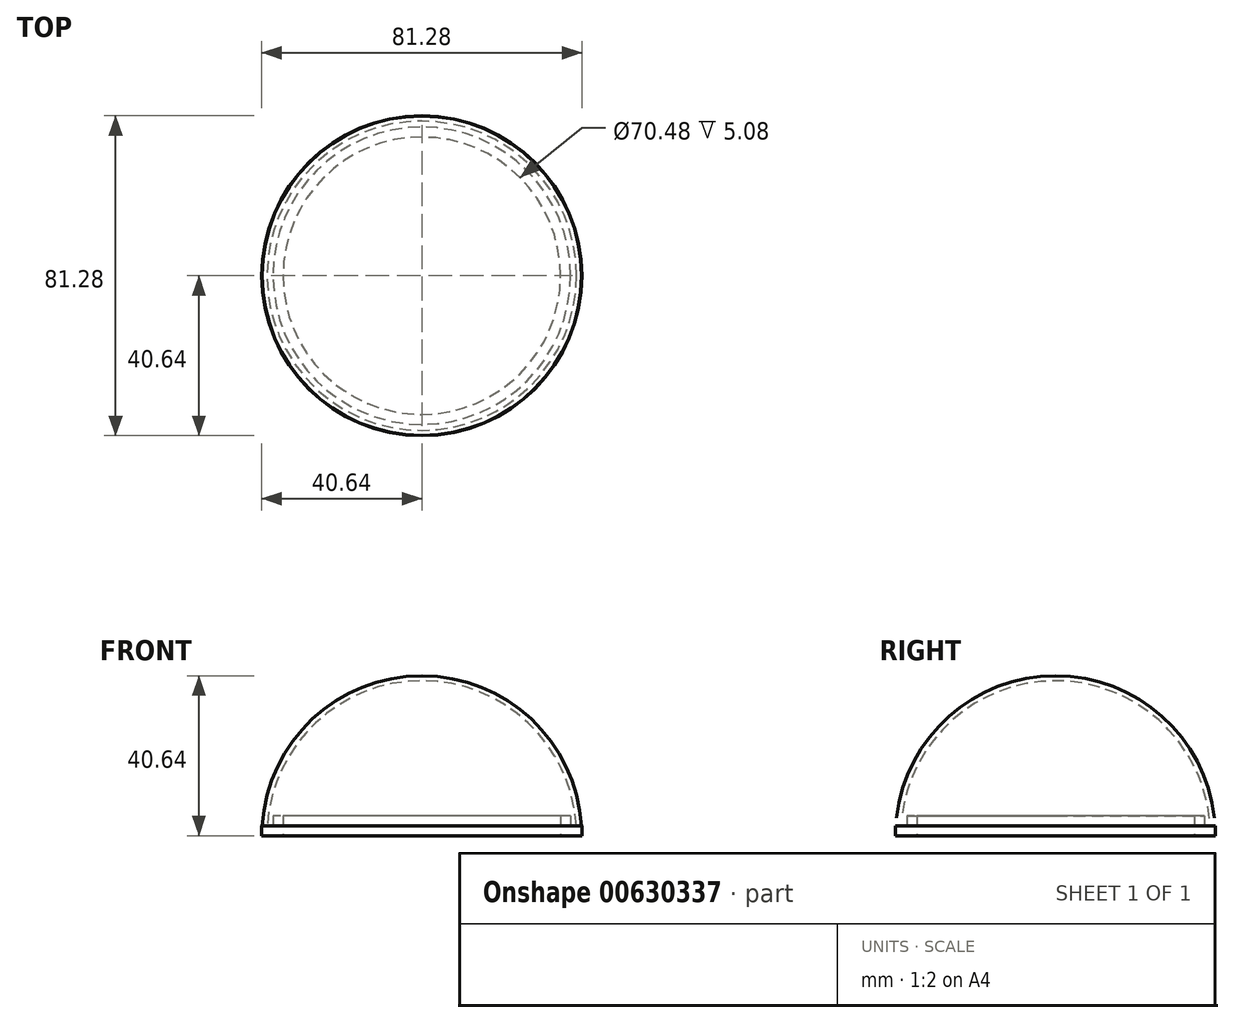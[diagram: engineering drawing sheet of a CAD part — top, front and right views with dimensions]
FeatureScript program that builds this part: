
annotation { "Feature Type Name" : "Feature", "Feature Type Description" : "" }
export const myFeature = defineFeature(function(context is Context, id is Id, definition is map)
    precondition{}
    {
        {
            var Q0;
            Q0=qCreatedBy(makeId("Top.planeOp"),FACE);
            var sketch = newSketch(context, id + "F0", { "sketchPlane" : qUnion([Q0])});
            skCircle(sketch, "E0", {"center": v(0, 0) * mm, "radius": 35.24 * mm});
            skCircle(sketch, "E1", {"center": v(0, 0) * mm, "radius": 40.64 * mm});
            skCircle(sketch, "E2", {"center": v(0, 0) * mm, "radius": 37.78 * mm});
            skLineSegment(sketch, "E3", {"start": v(0, 63.56) * mm, "end": v(0, -49.2) * mm});
            skCircle(sketch, "E4", {"center": v(0, 0) * mm, "radius": 39.37 * mm});
            skSolve(sketch);
        }
        {
            var Q0;
            {var subQ0=sQuery(id+"F0.wireOp",EDGE,"E3");var subQ1=sQuery(id+"F0.wireOp",EDGE,"E1");var subQ2=makeQuery(id+"F0.imprint","INTERSECT",VERTEX,{"disambiguationData":[OD(0.0)],"derivedFrom":[subQ1,subQ0]});Q0=makeQuery(id+"F0.imprint","IMPRINT",FACE,{"disambiguationData":[TD([[makeQuery(id+"F0.imprint","IMPRINT",EDGE,{"disambiguationData":[TD([[subQ2,-1.0]])],"derivedFrom":subQ1}),1.0]])]});}
            var Q1;
            Q1=sQuery(id+"F0.wireOp",EDGE,"E3");
            revolve(context, id + "F1", {"entities" : qUnion([Q0]), "axis" : qUnion([Q1]), "revolveType" : RevolveType.ONE_DIRECTION, "angle" : 180 * degree});
        }
        {
            var Q0;
            {var subQ0=sQuery(id+"F0.wireOp",EDGE,"E3");var subQ1=sQuery(id+"F0.wireOp",EDGE,"E1");var subQ2=makeQuery(id+"F0.imprint","INTERSECT",VERTEX,{"disambiguationData":[OD(0.0)],"derivedFrom":[subQ1,subQ0]});Q0=makeQuery(id+"F0.imprint","IMPRINT",FACE,{"disambiguationData":[TD([[makeQuery(id+"F0.imprint","IMPRINT",EDGE,{"disambiguationData":[TD([[subQ2,1.0]])],"derivedFrom":subQ1}),1.0]])]});}
            var Q1;
            {var subQ0=sQuery(id+"F0.wireOp",EDGE,"E3");var subQ1=sQuery(id+"F0.wireOp",EDGE,"E0");var subQ2=makeQuery(id+"F0.imprint","INTERSECT",VERTEX,{"disambiguationData":[OD(0.0)],"derivedFrom":[subQ1,subQ0]});Q1=makeQuery(id+"F0.imprint","IMPRINT",FACE,{"disambiguationData":[TD([[makeQuery(id+"F0.imprint","IMPRINT",EDGE,{"disambiguationData":[TD([[subQ2,1.0]])],"derivedFrom":subQ1}),-1.0]])]});}
            var Q2;
            {var subQ0=sQuery(id+"F0.wireOp",EDGE,"E3");var subQ1=sQuery(id+"F0.wireOp",EDGE,"E1");var subQ2=makeQuery(id+"F0.imprint","INTERSECT",VERTEX,{"disambiguationData":[OD(0.0)],"derivedFrom":[subQ1,subQ0]});Q2=makeQuery(id+"F0.imprint","IMPRINT",FACE,{"disambiguationData":[TD([[makeQuery(id+"F0.imprint","IMPRINT",EDGE,{"disambiguationData":[TD([[subQ2,-1.0]])],"derivedFrom":subQ1}),1.0]])]});}
            var Q3;
            {var subQ0=sQuery(id+"F0.wireOp",EDGE,"E3");var subQ1=sQuery(id+"F0.wireOp",EDGE,"E0");var subQ2=makeQuery(id+"F0.imprint","INTERSECT",VERTEX,{"disambiguationData":[OD(0.0)],"derivedFrom":[subQ1,subQ0]});Q3=makeQuery(id+"F0.imprint","IMPRINT",FACE,{"disambiguationData":[TD([[makeQuery(id+"F0.imprint","IMPRINT",EDGE,{"disambiguationData":[TD([[subQ2,-1.0]])],"derivedFrom":subQ1}),-1.0]])]});}
            var Q4;
            {var subQ0=sQuery(id+"F0.wireOp",EDGE,"E3");var subQ1=sQuery(id+"F0.wireOp",EDGE,"E2");var subQ2=makeQuery(id+"F0.imprint","INTERSECT",VERTEX,{"disambiguationData":[OD(0.0)],"derivedFrom":[subQ1,subQ0]});Q4=makeQuery(id+"F0.imprint","IMPRINT",FACE,{"disambiguationData":[TD([[makeQuery(id+"F0.imprint","IMPRINT",EDGE,{"disambiguationData":[TD([[subQ2,-1.0]])],"derivedFrom":subQ1}),-1.0]])]});}
            var Q5;
            {var subQ0=sQuery(id+"F0.wireOp",EDGE,"E3");var subQ1=sQuery(id+"F0.wireOp",EDGE,"E2");var subQ2=makeQuery(id+"F0.imprint","INTERSECT",VERTEX,{"disambiguationData":[OD(0.0)],"derivedFrom":[subQ1,subQ0]});Q5=makeQuery(id+"F0.imprint","IMPRINT",FACE,{"disambiguationData":[TD([[makeQuery(id+"F0.imprint","IMPRINT",EDGE,{"disambiguationData":[TD([[subQ2,1.0]])],"derivedFrom":subQ1}),-1.0]])]});}
            extrude(context, id + "F2", {"entities" : qUnion([Q0, Q1, Q2, Q3, Q4, Q5]), "operationType" : NewBodyOperationType.ADD, "depth" : 2.54 * mm, "offsetDistance" : 25.4 * mm});
        }
        {
            var Q0;
            {var subQ0=sQuery(id+"F0.wireOp",EDGE,"E3");var subQ1=sQuery(id+"F0.wireOp",EDGE,"E0");var subQ2=makeQuery(id+"F0.imprint","INTERSECT",VERTEX,{"disambiguationData":[OD(0.0)],"derivedFrom":[subQ1,subQ0]});Q0=makeQuery(id+"F0.imprint","IMPRINT",FACE,{"disambiguationData":[TD([[makeQuery(id+"F0.imprint","IMPRINT",EDGE,{"disambiguationData":[TD([[subQ2,1.0]])],"derivedFrom":subQ1}),-1.0]])]});}
            var Q1;
            {var subQ0=sQuery(id+"F0.wireOp",EDGE,"E3");var subQ1=sQuery(id+"F0.wireOp",EDGE,"E0");var subQ2=makeQuery(id+"F0.imprint","INTERSECT",VERTEX,{"disambiguationData":[OD(0.0)],"derivedFrom":[subQ1,subQ0]});Q1=makeQuery(id+"F0.imprint","IMPRINT",FACE,{"disambiguationData":[TD([[makeQuery(id+"F0.imprint","IMPRINT",EDGE,{"disambiguationData":[TD([[subQ2,-1.0]])],"derivedFrom":subQ1}),-1.0]])]});}
            extrude(context, id + "F3", {"entities" : qUnion([Q0, Q1]), "operationType" : NewBodyOperationType.ADD, "depth" : 5.08 * mm, "offsetDistance" : 25.4 * mm});
        }
    });
